# Revit family: Paper_Towel_Holder-Auto_Released-Whitehall-BestCare-WH1846B_Series
name_source: partatom
category: Specialty Equipment
units: mm (PartAtom-declared; Revit-internal decimal feet)

## family parameters
Cut with Voids When Loaded = Yes
Host = Face
OmniClass Number = 23.40.20.21
OmniClass Title = Toilet and Bath Specialties
Part Type = Normal
Room Calculation Point = No
Round Connector Dimension = Use Diameter
Shared = Yes

## types (3) — shared parameters
Assembly Code = C1030200
Default Elevation = 34"
Depth of Bury = 3 1/2"
Description = BestCare® Ligature-Resistant Spindle-Button Semi-Recessed Stainless Steel Paper Towel Holder
Height = 9"
Installation Type = Recessed Wall Mounted
Length = 15 1/4"
Manufacturer = Whitehall
Product Documentation Link = https://www.whitehallmfg.com
Product Page URL = https://www.whitehallmfg.com
URL = https://www.whitehallmfg.com

## per-type parameters (varying)
| type | Finish | Material | Type Comments |
| WH1846FA | Stainless Steel-Whitehall-Powder Coated White | Stainless Steel-Whitehall-Powder Coated White | Ligature-Resistant, Spindle Button, Semi-Recessed Paper Towel Holder (White) |
| WH1846A-FA | Stainless Steel-Whitehall-Powder Coated White | Stainless Steel-Whitehall-Powder Coated White | Ligature-Resistant, Spindle Button, Semi-Recessed Paper Towel Holder (White) |
| WH1846FA-SS | Stainless Steel-Whitehall-Satin | Stainless Steel-Whitehall-Satin | Ligature-Resistant, Spindle Button, Semi-Recessed Paper Towel Holder (Stainless Steel) |

note: column(s) folded — value = type name in every type: Model

## geometry (parser evidence)
native form markers: Sweep x3
no freeform markers — native parametric forms only
